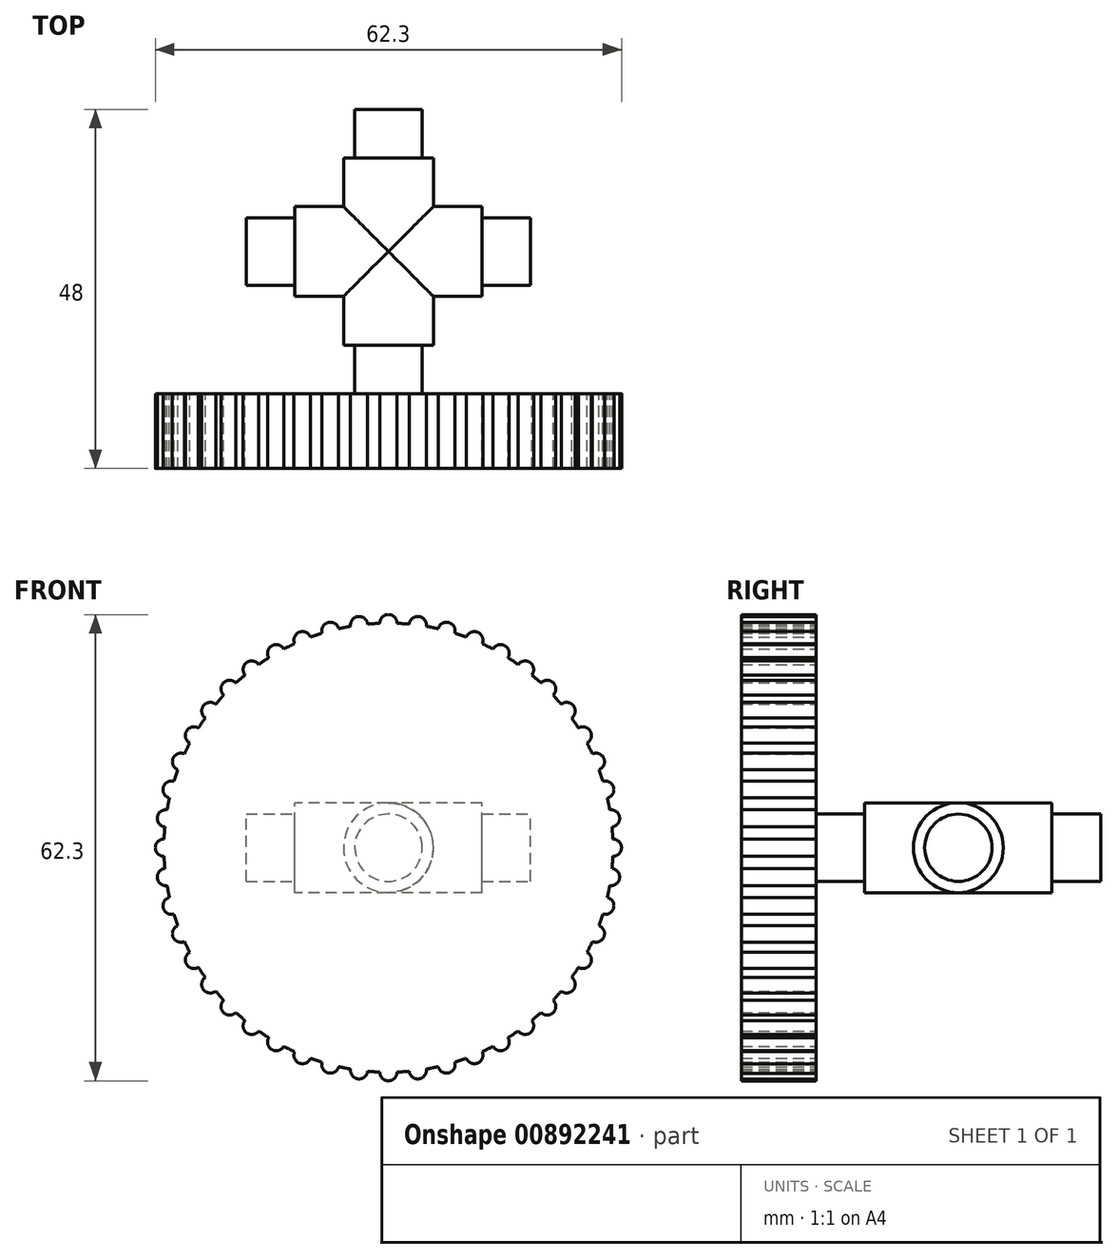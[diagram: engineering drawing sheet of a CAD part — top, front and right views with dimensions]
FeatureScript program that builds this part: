
annotation { "Feature Type Name" : "Feature", "Feature Type Description" : "" }
export const myFeature = defineFeature(function(context is Context, id is Id, definition is map)
    precondition{}
    {
        {
            var Q0;
            Q0=qCreatedBy(makeId("Front.planeOp"),FACE);
            var sketch = newSketch(context, id + "F0", { "sketchPlane" : qUnion([Q0])});
            skCircle(sketch, "E0", {"center": v(0, 0) * mm, "radius": 6 * mm});
            skSolve(sketch);
        }
        {
            var Q0;
            Q0=qSketchRegion(id+"F0",true);
            extrude(context, id + "F1", {"entities" : qUnion([Q0]), "endBound" : BoundingType.SYMMETRIC, "depth" : 25 * mm});
        }
        {
            var Q0;
            Q0=qCreatedBy(makeId("Right.planeOp"),FACE);
            var sketch = newSketch(context, id + "F2", { "sketchPlane" : qUnion([Q0])});
            skCircle(sketch, "E1", {"center": v(0, 0) * mm, "radius": 6 * mm});
            skSolve(sketch);
        }
        {
            var Q0;
            Q0=qSketchRegion(id+"F2",true);
            extrude(context, id + "F3", {"entities" : qUnion([Q0]), "operationType" : NewBodyOperationType.ADD, "endBound" : BoundingType.SYMMETRIC, "depth" : 25 * mm});
        }
        {
            var Q0;
            Q0=qCreatedBy(makeId("Front.planeOp"),FACE);
            cPlane(context, id + "F4", {"entities" : qUnion([Q0]), "cplaneType" : CPlaneType.OFFSET, "offset" : 19 * mm, "width" : 150 * mm, "height" : 150 * mm});
        }
        {
            var Q0;
            Q0=qCreatedBy(id+"F4.planeOp",FACE);
            var sketch = newSketch(context, id + "F5", { "sketchPlane" : qUnion([Q0])});
            skCircle(sketch, "E2", {"center": v(0, 0) * mm, "radius": 4.5 * mm});
            skSolve(sketch);
        }
        {
            var Q0;
            Q0=qSketchRegion(id+"F5",true);
            var Q1;
            Q1=makeQuery(id+"F5.imprint","IMPRINT",FACE,{"disambiguationData":[TD([[makeQuery(id+"F5.imprint","IMPRINT",EDGE,{"derivedFrom":sQuery(id+"F5.wireOp",EDGE,"E2")}),1.0]])]});
            extrude(context, id + "F6", {"entities" : qUnion([Q0, Q1]), "operationType" : NewBodyOperationType.ADD, "oppositeDirection" : true, "depth" : 38 * mm});
        }
        {
            var Q0;
            Q0=qCreatedBy(makeId("Right.planeOp"),FACE);
            cPlane(context, id + "F7", {"entities" : qUnion([Q0]), "cplaneType" : CPlaneType.OFFSET, "offset" : 19 * mm, "width" : 150 * mm, "height" : 150 * mm});
        }
        {
            var Q0;
            Q0=qCreatedBy(id+"F7.planeOp",FACE);
            var sketch = newSketch(context, id + "F8", { "sketchPlane" : qUnion([Q0])});
            skCircle(sketch, "E3", {"center": v(0, 0) * mm, "radius": 4.5 * mm});
            skSolve(sketch);
        }
        {
            var Q0;
            Q0=qSketchRegion(id+"F8",true);
            extrude(context, id + "F9", {"entities" : qUnion([Q0]), "operationType" : NewBodyOperationType.ADD, "oppositeDirection" : true, "depth" : 38 * mm});
        }
        {
            var Q0;
            Q0=makeQuery(id+"F6.opExtrude","CAP_FACE",FACE,{"disambiguationData":[OSD([sQuery(id+"F5.wireOp",EDGE,"E2")])],"isStart":true});
            var sketch = newSketch(context, id + "F10", { "sketchPlane" : qUnion([Q0])});
            skCircle(sketch, "E4", {"center": v(0, 0) * mm, "radius": 30 * mm});
            skCircle(sketch, "E5", {"center": v(0, 30) * mm, "radius": 1.15 * mm});
            skArc(sketch, "E6.41.0", {"start": v(1.15, 29.98) * mm, "mid": v(-0.8, 30.82) * mm, "end": v(0, 28.85) * mm});
            skArc(sketch, "E6.47.0", {"start": v(1.15, 29.98) * mm, "mid": v(0, 31.15) * mm, "end": v(-1.15, 29.98) * mm});
            skLineSegment(sketch, "E6.anchor1", {"start": v(0, 0) * mm, "end": v(0, 30) * mm, "construction": true});
            skLineSegment(sketch, "E6.anchor2", {"start": v(0, 0) * mm, "end": v(0, 30) * mm, "construction": true});
            skCircle(sketch, "E7.1.0", {"center": v(-3.92, 29.74) * mm, "radius": 1.15 * mm});
            skCircle(sketch, "E7.2.0", {"center": v(-7.76, 28.98) * mm, "radius": 1.15 * mm});
            skCircle(sketch, "E7.3.0", {"center": v(-11.48, 27.72) * mm, "radius": 1.15 * mm});
            skCircle(sketch, "E7.4.0", {"center": v(-15, 25.98) * mm, "radius": 1.15 * mm});
            skCircle(sketch, "E7.5.0", {"center": v(-18.26, 23.8) * mm, "radius": 1.15 * mm});
            skCircle(sketch, "E7.6.0", {"center": v(-21.21, 21.21) * mm, "radius": 1.15 * mm});
            skCircle(sketch, "E7.7.0", {"center": v(-23.8, 18.26) * mm, "radius": 1.15 * mm});
            skCircle(sketch, "E7.8.0", {"center": v(-25.98, 15) * mm, "radius": 1.15 * mm});
            skCircle(sketch, "E7.9.0", {"center": v(-27.72, 11.48) * mm, "radius": 1.15 * mm});
            skCircle(sketch, "E7.10.0", {"center": v(-28.98, 7.76) * mm, "radius": 1.15 * mm});
            skCircle(sketch, "E7.11.0", {"center": v(-29.74, 3.92) * mm, "radius": 1.15 * mm});
            skCircle(sketch, "E7.12.0", {"center": v(-30, 0) * mm, "radius": 1.15 * mm});
            skCircle(sketch, "E7.13.0", {"center": v(-29.74, -3.92) * mm, "radius": 1.15 * mm});
            skCircle(sketch, "E7.14.0", {"center": v(-28.98, -7.76) * mm, "radius": 1.15 * mm});
            skCircle(sketch, "E7.15.0", {"center": v(-27.72, -11.48) * mm, "radius": 1.15 * mm});
            skCircle(sketch, "E7.16.0", {"center": v(-25.98, -15) * mm, "radius": 1.15 * mm});
            skCircle(sketch, "E7.17.0", {"center": v(-23.8, -18.26) * mm, "radius": 1.15 * mm});
            skCircle(sketch, "E7.18.0", {"center": v(-21.21, -21.21) * mm, "radius": 1.15 * mm});
            skCircle(sketch, "E7.19.0", {"center": v(-18.26, -23.8) * mm, "radius": 1.15 * mm});
            skCircle(sketch, "E7.20.0", {"center": v(-15, -25.98) * mm, "radius": 1.15 * mm});
            skCircle(sketch, "E7.21.0", {"center": v(-11.48, -27.72) * mm, "radius": 1.15 * mm});
            skCircle(sketch, "E7.22.0", {"center": v(-7.76, -28.98) * mm, "radius": 1.15 * mm});
            skCircle(sketch, "E7.23.0", {"center": v(-3.92, -29.74) * mm, "radius": 1.15 * mm});
            skCircle(sketch, "E7.24.0", {"center": v(0, -30) * mm, "radius": 1.15 * mm});
            skCircle(sketch, "E7.25.0", {"center": v(3.92, -29.74) * mm, "radius": 1.15 * mm});
            skCircle(sketch, "E7.26.0", {"center": v(7.76, -28.98) * mm, "radius": 1.15 * mm});
            skCircle(sketch, "E7.27.0", {"center": v(11.48, -27.72) * mm, "radius": 1.15 * mm});
            skCircle(sketch, "E7.28.0", {"center": v(15, -25.98) * mm, "radius": 1.15 * mm});
            skCircle(sketch, "E7.29.0", {"center": v(18.26, -23.8) * mm, "radius": 1.15 * mm});
            skCircle(sketch, "E7.30.0", {"center": v(21.21, -21.21) * mm, "radius": 1.15 * mm});
            skCircle(sketch, "E7.31.0", {"center": v(23.8, -18.26) * mm, "radius": 1.15 * mm});
            skCircle(sketch, "E7.32.0", {"center": v(25.98, -15) * mm, "radius": 1.15 * mm});
            skCircle(sketch, "E7.33.0", {"center": v(27.72, -11.48) * mm, "radius": 1.15 * mm});
            skCircle(sketch, "E7.34.0", {"center": v(28.98, -7.76) * mm, "radius": 1.15 * mm});
            skCircle(sketch, "E7.35.0", {"center": v(29.74, -3.92) * mm, "radius": 1.15 * mm});
            skCircle(sketch, "E7.36.0", {"center": v(30, 0) * mm, "radius": 1.15 * mm});
            skCircle(sketch, "E7.37.0", {"center": v(29.74, 3.92) * mm, "radius": 1.15 * mm});
            skCircle(sketch, "E7.38.0", {"center": v(28.98, 7.76) * mm, "radius": 1.15 * mm});
            skCircle(sketch, "E7.39.0", {"center": v(27.72, 11.48) * mm, "radius": 1.15 * mm});
            skCircle(sketch, "E7.40.0", {"center": v(25.98, 15) * mm, "radius": 1.15 * mm});
            skCircle(sketch, "E7.41.0", {"center": v(23.8, 18.26) * mm, "radius": 1.15 * mm});
            skCircle(sketch, "E7.42.0", {"center": v(21.21, 21.21) * mm, "radius": 1.15 * mm});
            skCircle(sketch, "E7.43.0", {"center": v(18.26, 23.8) * mm, "radius": 1.15 * mm});
            skCircle(sketch, "E7.44.0", {"center": v(15, 25.98) * mm, "radius": 1.15 * mm});
            skCircle(sketch, "E8.1.45.0", {"center": v(11.48, 27.72) * mm, "radius": 1.15 * mm});
            skCircle(sketch, "E8.1.46.0", {"center": v(7.76, 28.98) * mm, "radius": 1.15 * mm});
            skCircle(sketch, "E9.1.47.0", {"center": v(3.92, 29.74) * mm, "radius": 1.15 * mm});
            skSolve(sketch);
        }
        {
            var Q0;
            Q0 = qSketchRegion(id + "F10", true);
            extrude(context, id + "F11", {"entities" : qUnion([Q0]), "operationType" : NewBodyOperationType.ADD, "depth" : 10 * mm, "offsetDistance" : 25 * mm});
        }
    });
